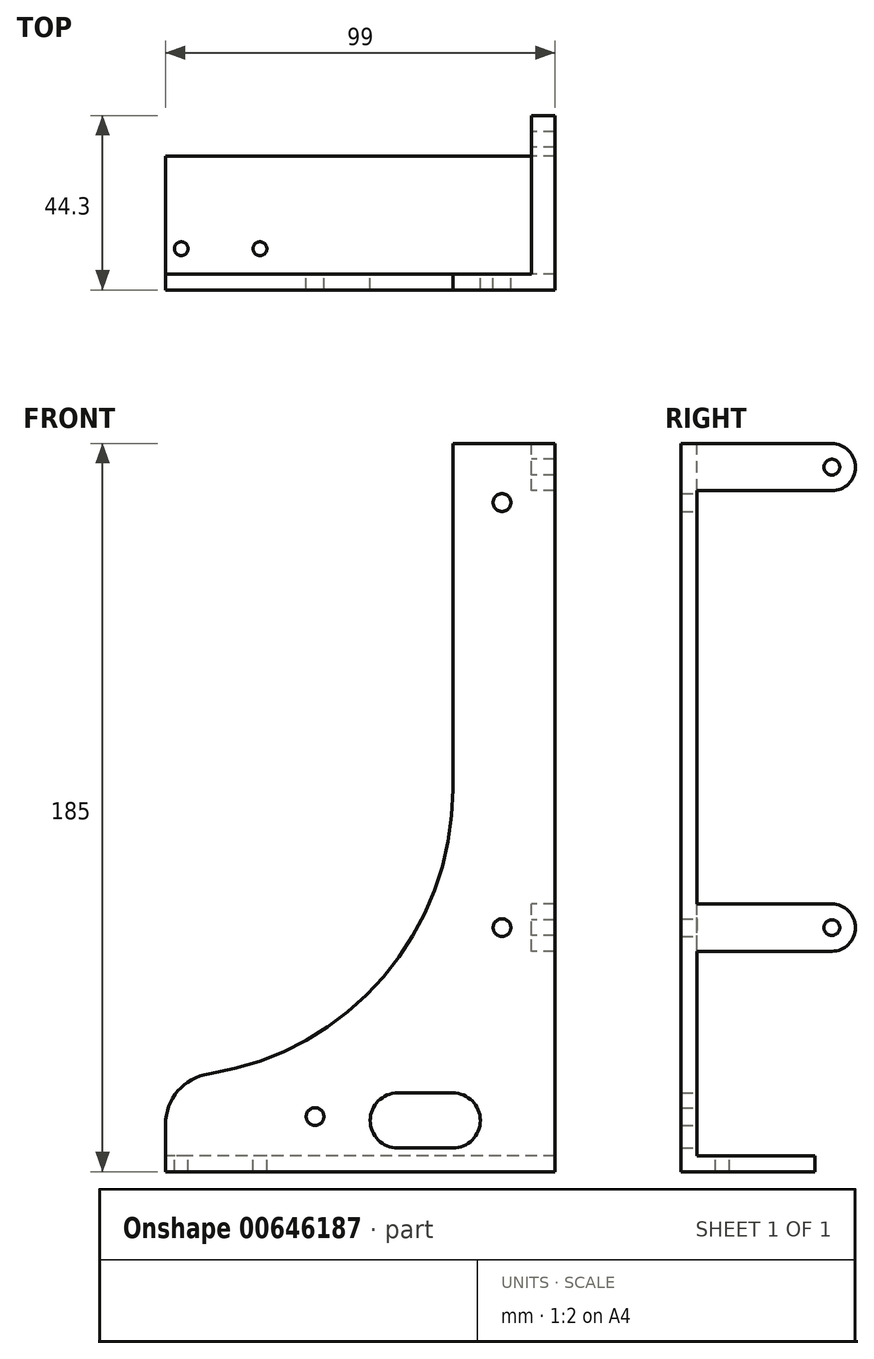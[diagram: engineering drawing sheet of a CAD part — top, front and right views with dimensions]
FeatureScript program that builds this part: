
annotation { "Feature Type Name" : "Feature", "Feature Type Description" : "" }
export const myFeature = defineFeature(function(context is Context, id is Id, definition is map)
    precondition{}
    {
        {
            var Q0;
            Q0=qCreatedBy(makeId("Right.planeOp"),FACE);
            var sketch = newSketch(context, id + "F0", { "sketchPlane" : qUnion([Q0])});
            skCircle(sketch, "E0", {"center": v(0, 175) * mm, "radius": 2 * mm});
            skCircle(sketch, "E1", {"center": v(0, 58) * mm, "radius": 2 * mm});
            skLineSegment(sketch, "E2", {"start": v(-34.3, 0) * mm, "end": v(-34.3, 181) * mm});
            skLineSegment(sketch, "E3", {"start": v(-34.3, 181) * mm, "end": v(6, 181) * mm});
            skLineSegment(sketch, "E4", {"start": v(6, 181) * mm, "end": v(6, 169) * mm});
            skLineSegment(sketch, "E5", {"start": v(6, 169) * mm, "end": v(-34.3, 169) * mm});
            skLineSegment(sketch, "E6.bottom", {"start": v(-34.3, 64) * mm, "end": v(6, 64) * mm});
            skLineSegment(sketch, "E6.top", {"start": v(-34.3, 52) * mm, "end": v(6, 52) * mm});
            skLineSegment(sketch, "E6.left", {"start": v(-34.3, 64) * mm, "end": v(-34.3, 52) * mm});
            skLineSegment(sketch, "E6.right", {"start": v(6, 64) * mm, "end": v(6, 52) * mm});
            skCircle(sketch, "E7.0", {"center": v(0, 58) * mm, "radius": 6 * mm});
            skCircle(sketch, "E8.0", {"center": v(0, 175) * mm, "radius": 6 * mm});
            skLineSegment(sketch, "E9", {"start": v(-38.3, 181) * mm, "end": v(-34.3, 181) * mm});
            skLineSegment(sketch, "E10", {"start": v(-34.3, 0) * mm, "end": v(-4.3, 0) * mm});
            skLineSegment(sketch, "E11.0", {"start": v(-38.3, -4) * mm, "end": v(-38.3, 181) * mm});
            skLineSegment(sketch, "E11.1", {"start": v(-38.3, -4) * mm, "end": v(-4.3, -4) * mm});
            skLineSegment(sketch, "E12", {"start": v(-4.3, -4) * mm, "end": v(-4.3, 0) * mm});
            skSolve(sketch);
        }
        {
            var Q0;
            {var subQ3=sQuery(id+"F0.wireOp",EDGE,"E9");Q0=makeQuery(id+"F0.imprint","IMPRINT",FACE,{"disambiguationData":[TD([[makeQuery(id+"F0.imprint","IMPRINT",EDGE,{"derivedFrom":subQ3}),-1.0]])]});}
            var Q1;
            {var subQ3=sQuery(id+"F0.wireOp",EDGE,"E5");var subQ5=sQuery(id+"F0.wireOp",EDGE,"E8.0");var subQ7=makeQuery(id+"F0.imprint","INTERSECT",VERTEX,{"derivedFrom":[subQ3,subQ5]});Q1=makeQuery(id+"F0.imprint","IMPRINT",FACE,{"disambiguationData":[TD([[makeQuery(id+"F0.imprint","IMPRINT",EDGE,{"disambiguationData":[TD([[subQ7,-1.0]])],"derivedFrom":subQ3}),-1.0]])]});}
            var Q2;
            {var subQ0=sQuery(id+"F0.wireOp",EDGE,"E6.bottom");var subQ1=sQuery(id+"F0.wireOp",EDGE,"E2");var subQ2=makeQuery(id+"F0.imprint","INTERSECT",VERTEX,{"derivedFrom":[subQ1,subQ0]});Q2=makeQuery(id+"F0.imprint","IMPRINT",FACE,{"disambiguationData":[TD([[makeQuery(id+"F0.imprint","IMPRINT",EDGE,{"disambiguationData":[TD([[subQ2,1.0]])],"derivedFrom":subQ1}),-1.0]])]});}
            var Q3;
            Q3=makeQuery(id+"F0.imprint","IMPRINT",FACE,{"disambiguationData":[TD([[makeQuery(id+"F0.imprint","IMPRINT",EDGE,{"derivedFrom":sQuery(id+"F0.wireOp",EDGE,"E0")}),-1.0]])]});
            var Q4;
            Q4=makeQuery(id+"F0.imprint","IMPRINT",FACE,{"disambiguationData":[TD([[makeQuery(id+"F0.imprint","IMPRINT",EDGE,{"derivedFrom":sQuery(id+"F0.wireOp",EDGE,"E1")}),-1.0]])]});
            extrude(context, id + "F1", {"entities" : qUnion([Q0, Q1, Q2, Q3, Q4]), "depth" : 6 * mm, "offsetDistance" : 25 * mm});
        }
        {
            var Q0;
            {var subQ3=sQuery(id+"F0.wireOp",EDGE,"E9");Q0=makeQuery(id+"F0.imprint","IMPRINT",FACE,{"disambiguationData":[TD([[makeQuery(id+"F0.imprint","IMPRINT",EDGE,{"derivedFrom":subQ3}),-1.0]])]});}
            extrude(context, id + "F2", {"entities" : qUnion([Q0]), "operationType" : NewBodyOperationType.ADD, "oppositeDirection" : true, "depth" : 93 * mm, "offsetDistance" : 25 * mm});
        }
        {
            var Q0;
            {var subQ0=sQuery(id+"F0.wireOp",EDGE,"E10");Q0=makeQuery(id+"F2.boolean.opBoolean","MERGE",FACE,{"derivedFrom":[makeQuery(id+"F1.opExtrude","SWEPT_FACE",FACE,{"disambiguationData":[OSD([subQ0])]}),makeQuery(id+"F2.opExtrude","SWEPT_FACE",FACE,{"disambiguationData":[OSD([subQ0])]})]});}
            var sketch = newSketch(context, id + "F3", { "sketchPlane" : qUnion([Q0])});
            skCircle(sketch, "E13", {"center": v(-69, -27.8) * mm, "radius": 1.75 * mm});
            skLineSegment(sketch, "E14", {"start": v(0, -27.8) * mm, "end": v(-93, -27.8) * mm, "construction": true});
            skCircle(sketch, "E15", {"center": v(-89, -27.8) * mm, "radius": 1.75 * mm});
            skSolve(sketch);
        }
        {
            var Q0;
            {var subQ3=sQuery(id+"F0.wireOp",EDGE,"E9");Q0=makeQuery(id+"F0.imprint","IMPRINT",FACE,{"disambiguationData":[TD([[makeQuery(id+"F0.imprint","IMPRINT",EDGE,{"derivedFrom":subQ3}),-1.0]])]});}
            extrude(context, id + "F4", {"entities" : qUnion([Q0]), "operationType" : NewBodyOperationType.ADD, "oppositeDirection" : true, "depth" : 25 * mm, "offsetDistance" : 25 * mm});
        }
        {
            var Q0;
            Q0=makeQuery(id+"F3.imprint","IMPRINT",FACE,{"disambiguationData":[TD([[makeQuery(id+"F3.imprint","IMPRINT",EDGE,{"derivedFrom":sQuery(id+"F3.wireOp",EDGE,"E15")}),1.0]])]});
            var Q1;
            Q1=makeQuery(id+"F3.imprint","IMPRINT",FACE,{"disambiguationData":[TD([[makeQuery(id+"F3.imprint","IMPRINT",EDGE,{"derivedFrom":sQuery(id+"F3.wireOp",EDGE,"E13")}),1.0]])]});
            extrude(context, id + "F5", {"entities" : qUnion([Q0, Q1]), "operationType" : NewBodyOperationType.REMOVE, "endBound" : BoundingType.THROUGH_ALL, "oppositeDirection" : true, "depth" : 25 * mm, "offsetDistance" : 25 * mm});
        }
        {
            var Q0;
            {var subQ0=sQuery(id+"F0.wireOp",EDGE,"E2");Q0=makeQuery(id+"F2.boolean.opBoolean","MERGE",FACE,{"derivedFrom":[makeQuery(id+"F1.opExtrude","SWEPT_FACE",FACE,{"disambiguationData":[OSD([subQ0]),TDD([makeQuery(id+"F0.imprint","IMPRINT",EDGE,{"disambiguationData":[TD([[makeQuery(id+"F0.imprint","INTERSECT",VERTEX,{"derivedFrom":[subQ0,sQuery(id+"F0.wireOp",EDGE,"E6.bottom")]}),-1.0]])],"derivedFrom":subQ0})])]}),makeQuery(id+"F1.opExtrude","SWEPT_FACE",FACE,{"disambiguationData":[OSD([subQ0]),TDD([makeQuery(id+"F0.imprint","IMPRINT",EDGE,{"disambiguationData":[TD([[makeQuery(id+"F0.imprint","INTERSECT",VERTEX,{"derivedFrom":[subQ0,sQuery(id+"F0.wireOp",EDGE,"E6.top")]}),1.0]])],"derivedFrom":subQ0})])]}),makeQuery(id+"F2.opExtrude","SWEPT_FACE",FACE,{"disambiguationData":[OSD([subQ0])]})]});}
            var sketch = newSketch(context, id + "F6", { "sketchPlane" : qUnion([Q0])});
            skLineSegment(sketch, "E16.bottom", {"start": v(93, 181) * mm, "end": v(20, 181) * mm});
            skLineSegment(sketch, "E16.top", {"start": v(93, 20) * mm, "end": v(20, 20) * mm});
            skLineSegment(sketch, "E16.left", {"start": v(93, 181) * mm, "end": v(93, 20) * mm});
            skLineSegment(sketch, "E16.right", {"start": v(20, 181) * mm, "end": v(20, 20) * mm});
            skCircle(sketch, "E17", {"center": v(20, 9) * mm, "radius": 7 * mm});
            skCircle(sketch, "E18", {"center": v(34, 9) * mm, "radius": 7 * mm});
            skLineSegment(sketch, "E19", {"start": v(34, 2) * mm, "end": v(20, 2) * mm});
            skLineSegment(sketch, "E20", {"start": v(20, 16) * mm, "end": v(34, 16) * mm});
            skLineSegment(sketch, "E21", {"start": v(7.5, 181) * mm, "end": v(7.5, 0) * mm, "construction": true});
            skCircle(sketch, "E22", {"center": v(7.5, 166) * mm, "radius": 2.25 * mm});
            skCircle(sketch, "E23", {"center": v(7.5, 58) * mm, "radius": 2.25 * mm});
            skCircle(sketch, "E24", {"center": v(55, 10) * mm, "radius": 2.25 * mm});
            skSolve(sketch);
        }
        {
            var Q0;
            Q0 = qSketchRegion(id + "F6", true);
            extrude(context, id + "F7", {"entities" : qUnion([Q0]), "operationType" : NewBodyOperationType.REMOVE, "endBound" : BoundingType.THROUGH_ALL, "oppositeDirection" : true, "depth" : 25 * mm, "offsetDistance" : 25 * mm});
        }
        {
            var Q0;
            Q0=makeQuery(id+"F7.boolean.opBoolean","COPY",EDGE,{"derivedFrom":makeQuery(id+"F7.opExtrude","SWEPT_EDGE",EDGE,{"disambiguationData":[OSD([sQuery(id+"F6.wireOp",EDGE,"E16.top"),sQuery(id+"F6.wireOp",EDGE,"E16.right")])]})});
            fillet(context, id + "F8", {"entities" : qUnion([Q0]), "radius" : 73.15 * mm, "tangentPropagation" : true, "allowEdgeOverflow" : false});
        }
        {
            var Q0;
            Q0=makeQuery(id+"F7.boolean.opBoolean","COPY",EDGE,{"derivedFrom":makeQuery(id+"F7.opExtrude","SWEPT_EDGE",EDGE,{"disambiguationData":[OSD([sQuery(id+"F0.wireOp",EDGE,"E2"),sQuery(id+"F0.wireOp",EDGE,"E6.left"),sQuery(id+"F6.wireOp",EDGE,"E16.top"),sQuery(id+"F6.wireOp",EDGE,"E16.left")])]})});
            var Q1;
            Q1=makeQuery(id+"F7.boolean.opBoolean","COPY",EDGE,{"derivedFrom":makeQuery(id+"F7.opExtrude","SWEPT_EDGE",EDGE,{"disambiguationData":[OSD([sQuery(id+"F0.wireOp",EDGE,"E2"),sQuery(id+"F0.wireOp",EDGE,"E3"),sQuery(id+"F0.wireOp",EDGE,"E9"),sQuery(id+"F6.wireOp",EDGE,"E16.bottom"),sQuery(id+"F6.wireOp",EDGE,"E16.right")])]})});
            var Q2;
            Q2=makeQuery(id+"F8.opFillet","BLEND_EDGE",EDGE,{"blendedFrom":[makeQuery(id+"F7.boolean.opBoolean","COPY",EDGE,{"derivedFrom":makeQuery(id+"F7.opExtrude","SWEPT_EDGE",EDGE,{"disambiguationData":[OSD([sQuery(id+"F6.wireOp",EDGE,"E16.top"),sQuery(id+"F6.wireOp",EDGE,"E16.right")])]})}),makeQuery(id+"F2.opExtrude","CAP_FACE",FACE,{"disambiguationData":[OSD([sQuery(id+"F0.wireOp",EDGE,"E2"),sQuery(id+"F0.wireOp",EDGE,"E9"),sQuery(id+"F0.wireOp",EDGE,"E10"),sQuery(id+"F0.wireOp",EDGE,"E11.0"),sQuery(id+"F0.wireOp",EDGE,"E11.1"),sQuery(id+"F0.wireOp",EDGE,"E12")])],"isStart":false})],"blendedInto":[makeQuery(id+"F2.opExtrude","CAP_FACE",FACE,{"disambiguationData":[OSD([sQuery(id+"F0.wireOp",EDGE,"E2"),sQuery(id+"F0.wireOp",EDGE,"E9"),sQuery(id+"F0.wireOp",EDGE,"E10"),sQuery(id+"F0.wireOp",EDGE,"E11.0"),sQuery(id+"F0.wireOp",EDGE,"E11.1"),sQuery(id+"F0.wireOp",EDGE,"E12")])],"isStart":false})]});
            fillet(context, id + "F9", {"entities" : qUnion([Q0, Q1, Q2]), "radius" : 13 * mm, "tangentPropagation" : true, "allowEdgeOverflow" : false});
        }
    });
